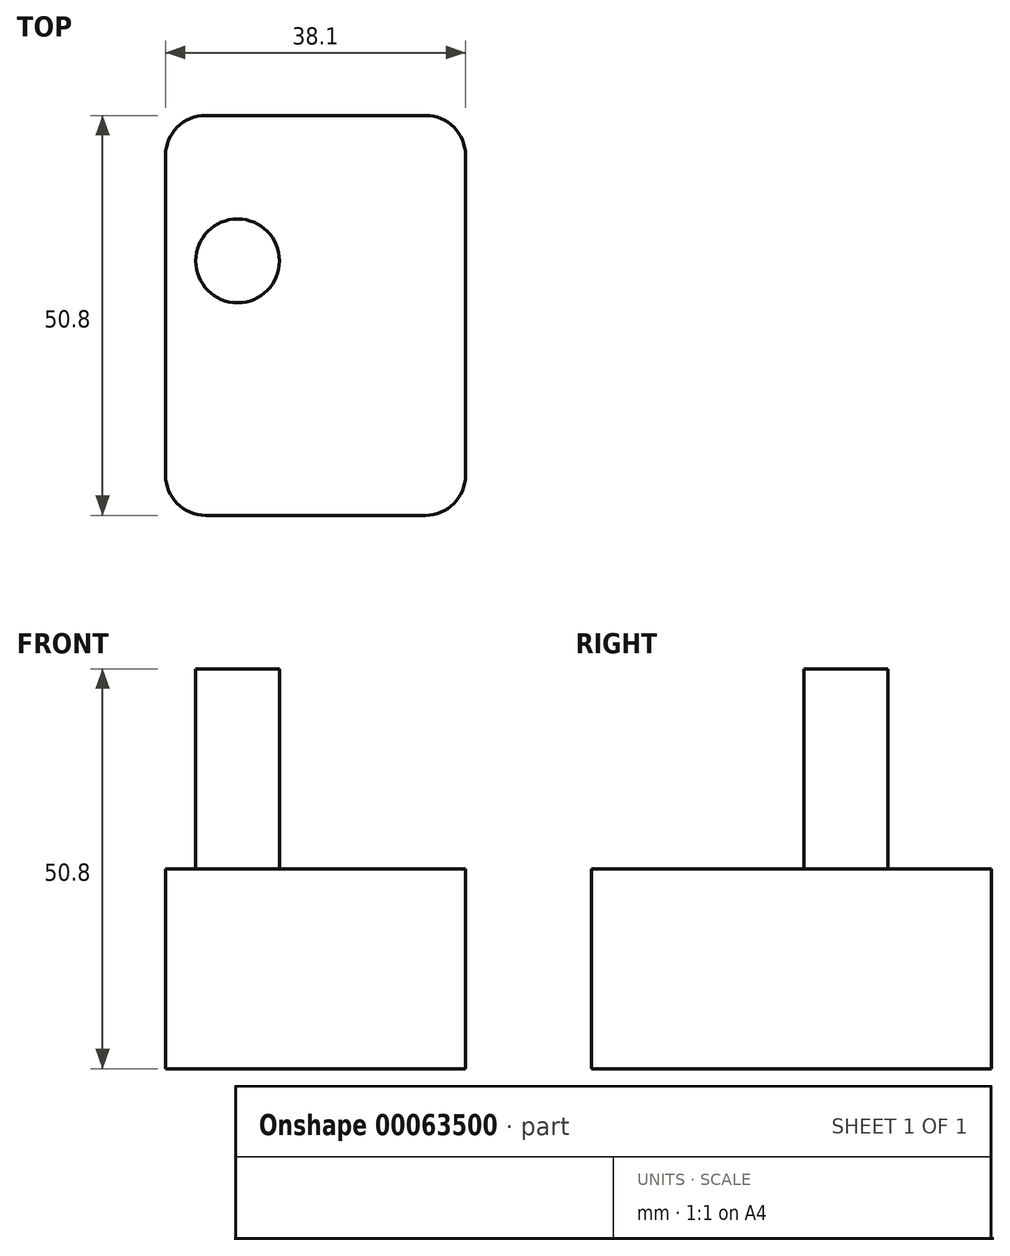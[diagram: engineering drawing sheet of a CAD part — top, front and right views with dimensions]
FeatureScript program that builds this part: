
annotation { "Feature Type Name" : "Feature", "Feature Type Description" : "" }
export const myFeature = defineFeature(function(context is Context, id is Id, definition is map)
    precondition{}
    {
        {
            var Q0;
            Q0=qCreatedBy(makeId("Top.planeOp"),FACE);
            var sketch = newSketch(context, id + "F0", { "sketchPlane" : qUnion([Q0])});
            skLineSegment(sketch, "E0.rect.bottom", {"start": v(-19.05, 25.4) * mm, "end": v(19.05, 25.4) * mm});
            skLineSegment(sketch, "E0.rect.top", {"start": v(-19.05, -25.4) * mm, "end": v(19.05, -25.4) * mm});
            skLineSegment(sketch, "E0.rect.left", {"start": v(-19.05, 25.4) * mm, "end": v(-19.05, -25.4) * mm});
            skLineSegment(sketch, "E0.rect.right", {"start": v(19.05, 25.4) * mm, "end": v(19.05, -25.4) * mm});
            skPoint(sketch, "E0.rect.middle", {"position": v(0, 0) * mm});
            skSolve(sketch);
        }
        {
            var Q0;
            Q0 = qSketchRegion(id + "F0", true);
            extrude(context, id + "F1", {"entities" : qUnion([Q0]), "depth" : 25.4 * mm});
        }
        {
            var Q0;
            Q0=makeQuery(id+"F1.opExtrude","CAP_FACE",FACE,{"disambiguationData":[OSD([sQuery(id+"F0.wireOp",EDGE,"E0.rect.bottom"),sQuery(id+"F0.wireOp",EDGE,"E0.rect.top"),sQuery(id+"F0.wireOp",EDGE,"E0.rect.left"),sQuery(id+"F0.wireOp",EDGE,"E0.rect.right")])],"isStart":false});
            var sketch = newSketch(context, id + "F2", { "sketchPlane" : qUnion([Q0])});
            skCircle(sketch, "E1", {"center": v(-9.9, 6.92) * mm, "radius": 5.32 * mm});
            skSolve(sketch);
        }
        {
            var Q0;
            Q0 = qSketchRegion(id + "F2", true);
            extrude(context, id + "F3", {"entities" : qUnion([Q0]), "operationType" : NewBodyOperationType.ADD, "depth" : 25.4 * mm});
        }
        {
            var Q0;
            Q0=makeQuery(id+"F1.opExtrude","SWEPT_EDGE",EDGE,{"disambiguationData":[OSD([sQuery(id+"F0.wireOp",EDGE,"E0.rect.top"),sQuery(id+"F0.wireOp",EDGE,"E0.rect.left")])]});
            var Q1;
            Q1=makeQuery(id+"F1.opExtrude","SWEPT_EDGE",EDGE,{"disambiguationData":[OSD([sQuery(id+"F0.wireOp",EDGE,"E0.rect.top"),sQuery(id+"F0.wireOp",EDGE,"E0.rect.right")])]});
            var Q2;
            Q2=makeQuery(id+"F1.opExtrude","SWEPT_EDGE",EDGE,{"disambiguationData":[OSD([sQuery(id+"F0.wireOp",EDGE,"E0.rect.bottom"),sQuery(id+"F0.wireOp",EDGE,"E0.rect.left")])]});
            var Q3;
            Q3=makeQuery(id+"F1.opExtrude","SWEPT_EDGE",EDGE,{"disambiguationData":[OSD([sQuery(id+"F0.wireOp",EDGE,"E0.rect.bottom"),sQuery(id+"F0.wireOp",EDGE,"E0.rect.right")])]});
            fillet(context, id + "F4", {"entities" : qUnion([Q0, Q1, Q2, Q3]), "radius" : 5.08 * mm, "tangentPropagation" : true, "allowEdgeOverflow" : false});
        }
    });
